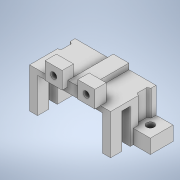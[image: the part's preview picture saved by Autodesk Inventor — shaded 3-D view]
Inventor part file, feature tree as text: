
AUTODESK INVENTOR PART (.ipt)
format: ipt  version: 2022 (Build 260153000, 153)  size: 233,472 bytes
history: native  units: mm
features: extrude x5, sketch x4, other x1
ambient origin geometry x8: Origin, YZ Plane, XZ Plane, XY Plane, X Axis, Y Axis, Z Axis, Center Point
bodies: Body1 (feature_tree)
feature tree (10):
  other  "FS90R.ipt"
  sketch  "スケッチ2"
  extrude  "ベース"  Depth=10.0mm
  extrude  "タブ切欠き"  Depth=12.1mm
  extrude  "マウント"  Depth=22.5mm
  extrude  "基板マウントタブ"  Depth=0.2mm
  extrude  "押し出し6"  Depth=0.2mm
  sketch  "スケッチ3"
  sketch  "スケッチ4"
  sketch  "スケッチ5"
